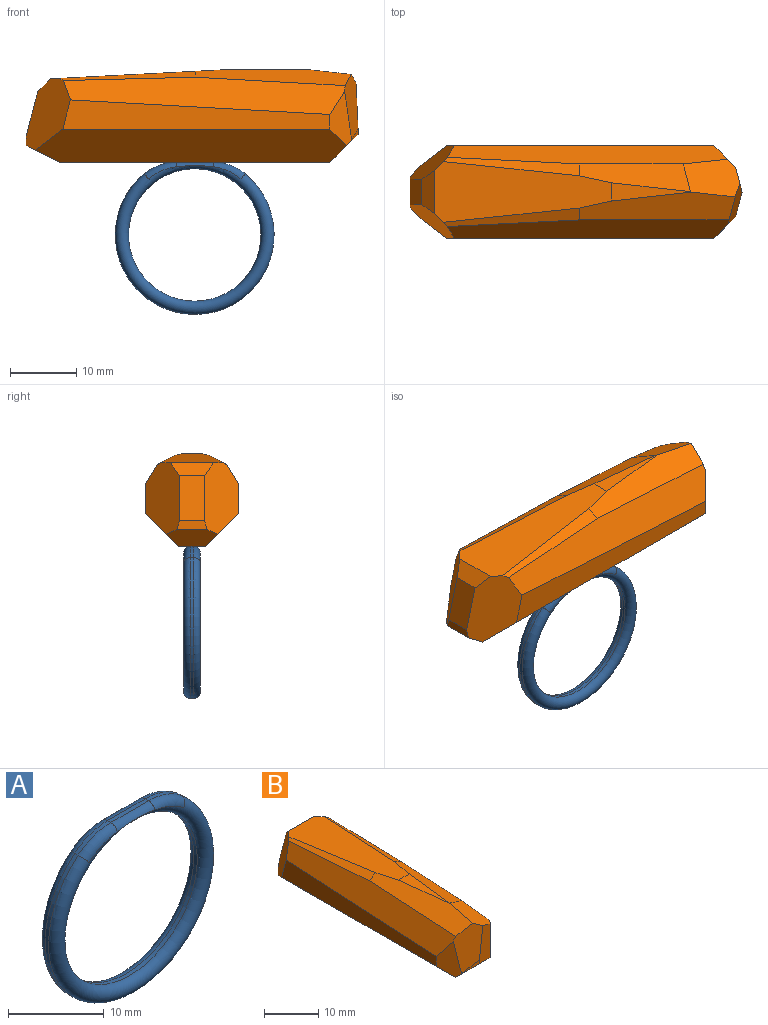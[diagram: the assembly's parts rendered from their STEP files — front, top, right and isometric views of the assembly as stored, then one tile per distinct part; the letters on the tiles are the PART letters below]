
ASSEMBLY  parts=2 mates=1
PART A: 13 faces, bbox 26x2.5x26 mm
  f0: plane 5.57x0.5mm, normal (0,0,1), area 2.8mm2, adj f3,f4,f8,f12
  f1: cylinder r=10mm len=20mm, axis (0,1,0), area 31.4mm2, adj f5,f9
  f2: cylinder r=12mm len=24mm, axis (0,1,0), area 29.4mm2, adj f3,f4,f5,f9
  f3: cylinder r=7.62mm len=4.85mm, axis (0,1,0), area 2.6mm2, adj f0,f2,f7,f10
  f4: cylinder r=7.62mm len=4.85mm, axis (0,1,0), area 2.6mm2, adj f0,f2,f6,f11
  f5: torus R=11mm, axis (0,-1,0), area 187.9mm2, adj f1,f2,f6,f7,f8
  f6: torus R=6.62mm, axis (0,-1,0), area 7.1mm2, adj f4,f5,f8
  f7: torus R=6.62mm, axis (0,-1,0), area 7.1mm2, adj f3,f5,f8
  f8: cylinder r=1mm len=5.57mm, axis (1,0,0), area 6.2mm2, adj f0,f5,f6,f7
  f9: torus R=11mm, axis (0,-1,0), area 187.9mm2, adj f1,f2,f10,f11,f12
  f10: torus R=6.62mm, axis (0,-1,0), area 7.1mm2, adj f3,f9,f12
  f11: torus R=6.62mm, axis (0,-1,0), area 7.1mm2, adj f4,f9,f12
  f12: cylinder r=1mm len=5.57mm, axis (-1,0,0), area 6.2mm2, adj f0,f9,f10,f11
PART B: 26 faces, bbox 14x50.2x14 mm
  f0: plane 40.84x4mm, normal (0,0,-1), area 163.4mm2, adj f8,f12,f13,f16
  f1: plane 40.37x4.42mm, normal (1,0,0), area 132.9mm2, adj f6,f11,f12,f14
  f2: plane 12.11x2.75mm, normal (0,0,1), area 16.9mm2, adj f5,f20,f23,f25
  f3: plane 4.5x1.3mm, normal (0,1,0), area 5.4mm2, adj f9,f13,f14,f15
  f4: plane 20.54x2.8mm, normal (0.45,0,0.89), area 28.2mm2, adj f5,f11,f14,f23
  f5: plane 16.79x4.19mm, normal (0.45,-0.05,0.89), area 57.2mm2, adj f2,f4,f11,f23,f25
  f6: plane 8.37x3.28mm, normal (0.71,-0.71,0), area 27.7mm2, adj f1,f8,f10,f11,f12,f25
  f7: plane 6.53x1.88mm, normal (0,0.71,0.71), area 13.8mm2, adj f9,f14,f15,f23
  f8: plane 9x4.25mm, normal (0,-0.71,-0.71), area 37.2mm2, adj f0,f6,f10,f12,f16,f18,f19
  f9: plane 6.88x3.84mm, normal (0,0.97,0.25), area 27.3mm2, adj f3,f7,f14,f15
  f10: plane 8.8x3.72mm, normal (0.25,-0.97,0), area 26.1mm2, adj f6,f8,f18,f24,f25
  f11: plane 42.33x5.62mm, normal (0.85,-0.03,0.53), area 193.7mm2, adj f1,f4,f5,f6,f14,f25
  f12: plane 46.98x5mm, normal (0.71,0,-0.71), area 309.4mm2, adj f0,f1,f6,f8,f13,f14
  f13: plane 7.64x5.08mm, normal (0,0.45,-0.89), area 33.5mm2, adj f0,f3,f12,f14,f15,f16
  f14: plane 10.85x6.71mm, normal (0.71,0.68,0.18), area 64.8mm2, adj f1,f3,f4,f7,f9,f11,f12,f13
  f15: plane 10.85x6.71mm, normal (-0.71,0.68,0.18), area 64.8mm2, adj f3,f7,f9,f13,f16,f17,f21,f22
  f16: plane 46.98x5mm, normal (-0.71,0,-0.71), area 309.4mm2, adj f0,f8,f13,f15,f19,f22
  f17: plane 42.58x5.62mm, normal (-0.85,-0.03,0.53), area 198.5mm2, adj f15,f19,f20,f21,f22,f24
  f18: plane 3.72x1.88mm, normal (-0.25,-0.97,0), area 1.9mm2, adj f8,f10,f19,f24
  f19: plane 8.21x3.28mm, normal (-0.71,-0.71,0), area 22.3mm2, adj f8,f16,f17,f18,f22,f24
  f20: plane 23.53x4.21mm, normal (-0.45,-0.05,0.89), area 87mm2, adj f2,f17,f21,f23,f24,f25
  f21: plane 20.54x2.8mm, normal (-0.45,0,0.89), area 28.2mm2, adj f15,f17,f20,f23
  f22: plane 40.37x4.42mm, normal (-1,0,0), area 132.9mm2, adj f15,f16,f17,f19
  f23: plane 26.8x9.17mm, normal (0,0.05,1), area 173.8mm2, adj f2,f4,f5,f7,f14,f15,f20,f21
  f24: plane 9.9x5.98mm, normal (-0.29,-0.95,0.09), area 42.5mm2, adj f10,f17,f18,f19,f20,f25
  f25: plane 8.56x5.72mm, normal (0.46,-0.15,0.87), area 43.2mm2, adj f2,f5,f6,f10,f11,f20,f24
PLACE A t=(26.18,12.63,-4.13)mm
PLACE B rot(axis=(0,0,1),90deg) t=(26.68,11.38,13.87)mm
MATE fastened B.f0 <-> A.f0  axis (0,0,-1) through (26.18,11.38,6.87)mm
